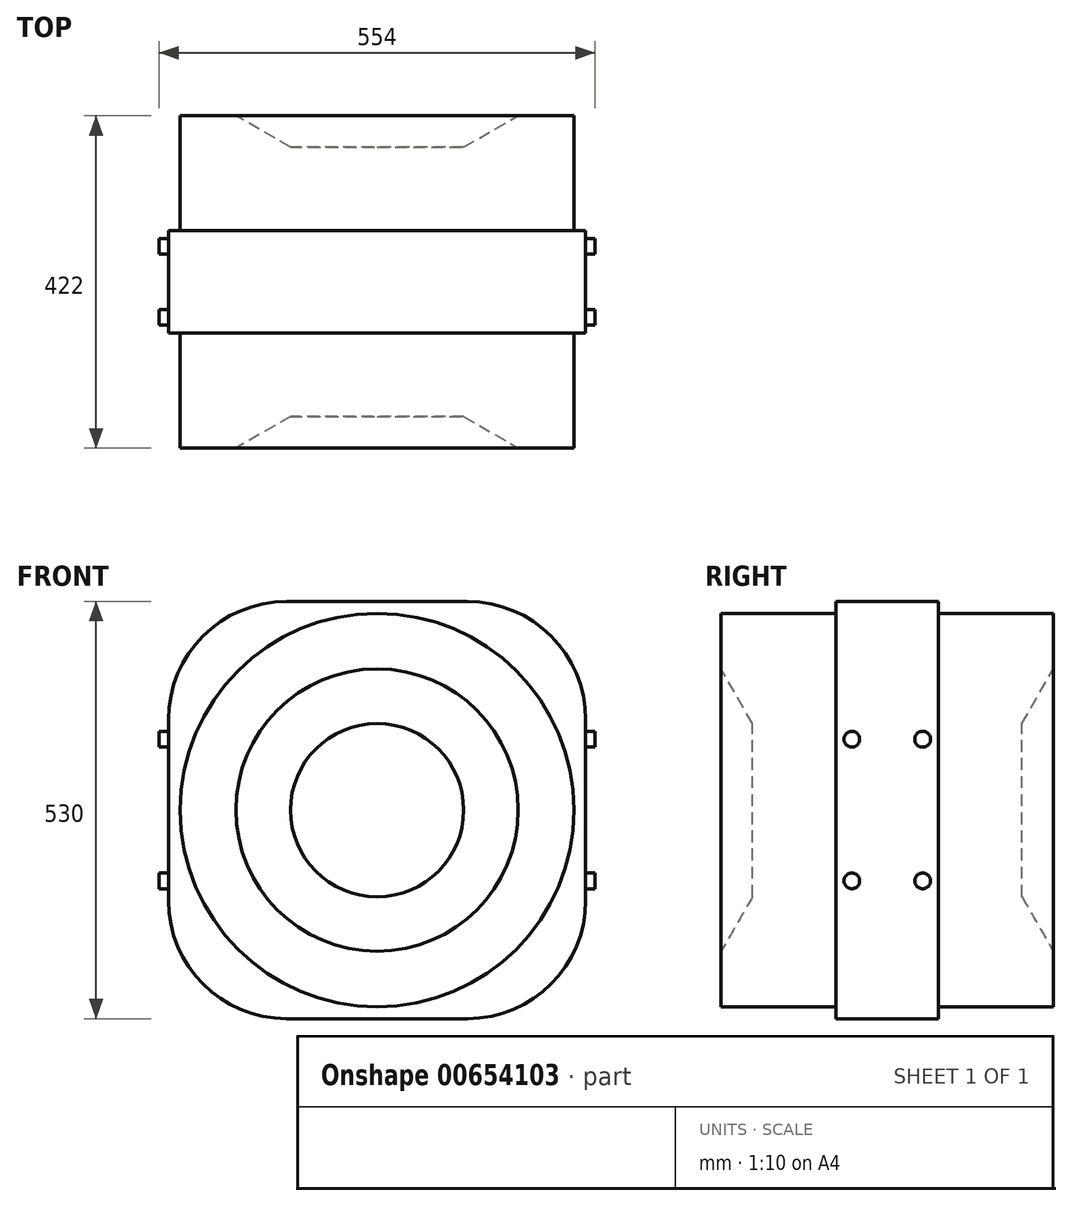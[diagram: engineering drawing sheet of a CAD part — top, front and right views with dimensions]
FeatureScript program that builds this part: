
annotation { "Feature Type Name" : "Feature", "Feature Type Description" : "" }
export const myFeature = defineFeature(function(context is Context, id is Id, definition is map)
    precondition{}
    {
        {
            var Q0;
            Q0=qCreatedBy(makeId("Front.planeOp"),FACE);
            var sketch = newSketch(context, id + "F0", { "sketchPlane" : qUnion([Q0])});
            skLineSegment(sketch, "E0.bottom", {"start": v(-265, 265) * mm, "end": v(265, 265) * mm});
            skLineSegment(sketch, "E0.top", {"start": v(-265, -265) * mm, "end": v(265, -265) * mm});
            skLineSegment(sketch, "E0.left", {"start": v(-265, 265) * mm, "end": v(-265, -265) * mm});
            skLineSegment(sketch, "E0.right", {"start": v(265, 265) * mm, "end": v(265, -265) * mm});
            skPoint(sketch, "E0.middle", {"position": v(0, 0) * mm});
            skCircle(sketch, "E1", {"center": v(0, 0) * mm, "radius": 250 * mm});
            skCircle(sketch, "E2", {"center": v(0, 0) * mm, "radius": 110 * mm});
            skSolve(sketch);
        }
        {
            var Q0;
            Q0 = qSketchRegion(id + "F0", true);
            extrude(context, id + "F1", {"entities" : qUnion([Q0]), "depth" : 130 / 2 * mm, "offsetDistance" : 25 * mm, "hasSecondDirection" : true, "secondDirectionOppositeDirection" : true, "secondDirectionDepth" : 65 * mm});
        }
        {
            var Q0;
            Q0=makeQuery(id+"F1.opExtrude","SWEPT_FACE",FACE,{"disambiguationData":[OSD([sQuery(id+"F0.wireOp",EDGE,"E0.right")])]});
            var sketch = newSketch(context, id + "F2", { "sketchPlane" : qUnion([Q0])});
            skLineSegment(sketch, "E3.bottom", {"start": v(-45, 90) * mm, "end": v(45, 90) * mm, "construction": true});
            skLineSegment(sketch, "E3.top", {"start": v(-45, -90) * mm, "end": v(45, -90) * mm, "construction": true});
            skLineSegment(sketch, "E3.left", {"start": v(-45, 90) * mm, "end": v(-45, -90) * mm, "construction": true});
            skLineSegment(sketch, "E3.right", {"start": v(45, 90) * mm, "end": v(45, -90) * mm, "construction": true});
            skPoint(sketch, "E3.middle", {"position": v(0, 0) * mm});
            skLineSegment(sketch, "E4", {"start": v(0, 265) * mm, "end": v(0, -265) * mm, "construction": true});
            skCircle(sketch, "E5", {"center": v(-45, 90) * mm, "radius": 10 * mm});
            skCircle(sketch, "E6", {"center": v(45, 90) * mm, "radius": 10 * mm});
            skCircle(sketch, "E7", {"center": v(45, -90) * mm, "radius": 10 * mm});
            skCircle(sketch, "E8", {"center": v(-45, -90) * mm, "radius": 10 * mm});
            skSolve(sketch);
        }
        {
            var Q0;
            Q0 = qSketchRegion(id + "F2", true);
            extrude(context, id + "F3", {"entities" : qUnion([Q0]), "operationType" : NewBodyOperationType.ADD, "depth" : 12 * mm, "offsetDistance" : 25 * mm, "hasSecondDirection" : true, "secondDirectionOppositeDirection" : true, "secondDirectionDepth" : (530 + 12) * mm});
        }
        {
            var Q0;
            Q0=makeQuery(id+"F1.opExtrude","SWEPT_EDGE",EDGE,{"disambiguationData":[OSD([sQuery(id+"F0.wireOp",EDGE,"E0.bottom"),sQuery(id+"F0.wireOp",EDGE,"E0.right")])]});
            var Q1;
            Q1=makeQuery(id+"F1.opExtrude","SWEPT_EDGE",EDGE,{"disambiguationData":[OSD([sQuery(id+"F0.wireOp",EDGE,"E0.bottom"),sQuery(id+"F0.wireOp",EDGE,"E0.left")])]});
            var Q2;
            Q2=makeQuery(id+"F1.opExtrude","SWEPT_EDGE",EDGE,{"disambiguationData":[OSD([sQuery(id+"F0.wireOp",EDGE,"E0.top"),sQuery(id+"F0.wireOp",EDGE,"E0.right")])]});
            var Q3;
            Q3=makeQuery(id+"F1.opExtrude","SWEPT_EDGE",EDGE,{"disambiguationData":[OSD([sQuery(id+"F0.wireOp",EDGE,"E0.top"),sQuery(id+"F0.wireOp",EDGE,"E0.left")])]});
            fillet(context, id + "F4", {"entities" : qUnion([Q0, Q1, Q2, Q3]), "radius" : 150 * mm, "tangentPropagation" : true, "allowEdgeOverflow" : false});
        }
        {
            var Q0;
            Q0=makeQuery(id+"F0.imprint","IMPRINT",FACE,{"disambiguationData":[TD([[makeQuery(id+"F0.imprint","IMPRINT",EDGE,{"derivedFrom":sQuery(id+"F0.wireOp",EDGE,"E1")}),1.0]])]});
            extrude(context, id + "F5", {"entities" : qUnion([Q0]), "operationType" : NewBodyOperationType.ADD, "depth" : 422 / 2 * mm, "offsetDistance" : 25 * mm, "hasSecondDirection" : true, "secondDirectionOppositeDirection" : true, "secondDirectionDepth" : 211 * mm});
        }
        {
            var Q0;
            Q0=makeQuery(id+"F0.imprint","IMPRINT",FACE,{"disambiguationData":[TD([[makeQuery(id+"F0.imprint","IMPRINT",EDGE,{"derivedFrom":sQuery(id+"F0.wireOp",EDGE,"E2")}),1.0]])]});
            extrude(context, id + "F6", {"entities" : qUnion([Q0]), "operationType" : NewBodyOperationType.ADD, "depth" : (422 / 2 - 40) * mm, "offsetDistance" : 25 * mm, "hasSecondDirection" : true, "secondDirectionOppositeDirection" : true, "secondDirectionDepth" : 171 * mm});
        }
        {
            var Q0;
            Q0=makeQuery(id+"F5.opExtrude","CAP_EDGE",EDGE,{"disambiguationData":[OSD([sQuery(id+"F0.wireOp",EDGE,"E2")])],"isStart":false});
            chamfer(context, id + "F7", {"entities" : qUnion([Q0]), "chamferType" : ChamferType.OFFSET_ANGLE, "width" : 40 * mm, "oppositeDirection" : false, "angle" : 60 * degree});
        }
        {
            var Q0;
            Q0=makeQuery(id+"F5.opExtrude","CAP_EDGE",EDGE,{"disambiguationData":[OSD([sQuery(id+"F0.wireOp",EDGE,"E2")])],"isStart":true});
            chamfer(context, id + "F8", {"entities" : qUnion([Q0]), "chamferType" : ChamferType.OFFSET_ANGLE, "width" : 40 * mm, "oppositeDirection" : true, "angle" : 60 * degree, "tangentPropagation" : true});
        }
    });
